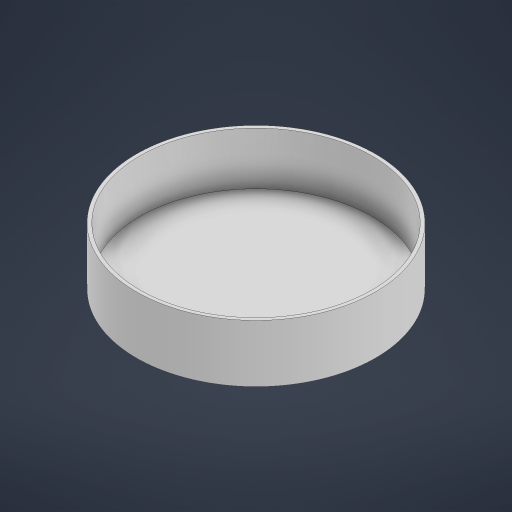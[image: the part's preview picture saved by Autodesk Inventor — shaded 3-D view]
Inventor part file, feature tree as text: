
AUTODESK INVENTOR PART (.ipt)
format: ipt  version: 2023 (Build 270158030, 158C)  size: 181,760 bytes
history: native  units: in
note: dims shown in document units (in); Inventor stores cm internally (conversion verified against a paired STEP export)
features: extrude x2, sketch x2
ambient origin geometry x8: Origin, YZ Plane, XZ Plane, XY Plane, X Axis, Y Axis, Z Axis, Center Point
bodies: Body1 (feature_tree)
feature tree (4):
  extrude  "Extrusion4"  Depth=2.3622in TaperAngle=0.0deg
  extrude  "Extrusion5"  Depth=2.1654in TaperAngle=0.0deg
  sketch  "Sketch22"  dims[d11=9.8425in d12=2.3622in d13=0.0in]
  sketch  "Sketch23"  dims[d14=9.5669in d15=2.1654in d16=0.0in]
